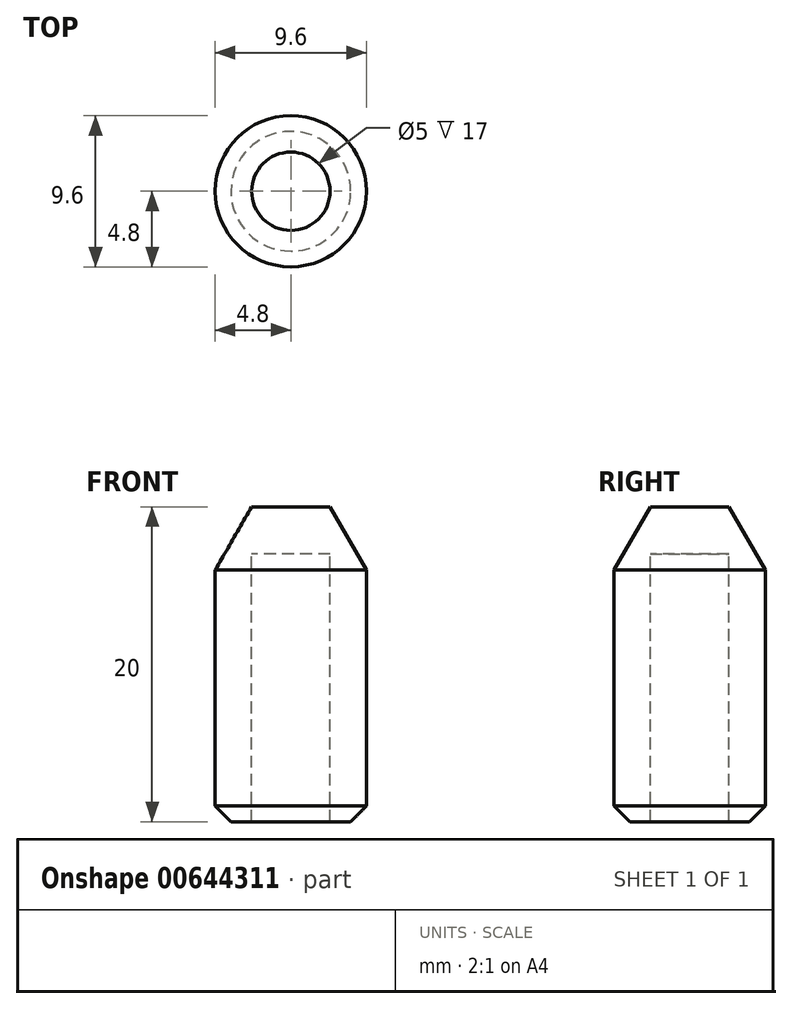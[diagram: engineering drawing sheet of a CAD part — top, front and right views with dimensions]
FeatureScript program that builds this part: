
annotation { "Feature Type Name" : "Feature", "Feature Type Description" : "" }
export const myFeature = defineFeature(function(context is Context, id is Id, definition is map)
    precondition{}
    {
        {
            var Q0;
            Q0=qCreatedBy(makeId("Right.planeOp"),FACE);
            var sketch = newSketch(context, id + "F0", { "sketchPlane" : qUnion([Q0])});
            skLineSegment(sketch, "E0", {"start": v(2.5, 0) * mm, "end": v(4.8, 0) * mm});
            skLineSegment(sketch, "E1", {"start": v(4.8, 0) * mm, "end": v(4.8, 20) * mm});
            skLineSegment(sketch, "E2", {"start": v(4.8, 20) * mm, "end": v(0, 20) * mm});
            skLineSegment(sketch, "E3", {"start": v(0, 42.87) * mm, "end": v(0, -12.23) * mm, "construction": true});
            skLineSegment(sketch, "E4", {"start": v(2.5, 0) * mm, "end": v(2.5, 17) * mm});
            skLineSegment(sketch, "E5", {"start": v(2.5, 17) * mm, "end": v(0, 17) * mm});
            skLineSegment(sketch, "E6", {"start": v(0, 20) * mm, "end": v(0, 17) * mm});
            skSolve(sketch);
        }
        {
            var Q0;
            Q0=qSketchRegion(id+"F0",true);
            var Q1;
            Q1=sQuery(id+"F0.wireOp",EDGE,"E3");
            revolve(context, id + "F1", {"entities" : qUnion([Q0]), "axis" : qUnion([Q1]), "revolveType" : RevolveType.FULL});
        }
        {
            var Q0;
            Q0=makeQuery(id+"F1.opRevolve","SWEPT_EDGE",EDGE,{"disambiguationData":[OSD([sQuery(id+"F0.wireOp",EDGE,"E0"),sQuery(id+"F0.wireOp",EDGE,"E1")])]});
            chamfer(context, id + "F2", {"entities" : qUnion([Q0]), "width" : 1 * mm, "tangentPropagation" : true});
        }
        {
            var Q0;
            Q0=makeQuery(id+"F1.opRevolve","SWEPT_EDGE",EDGE,{"disambiguationData":[OSD([sQuery(id+"F0.wireOp",EDGE,"E1"),sQuery(id+"F0.wireOp",EDGE,"E2")])]});
            chamfer(context, id + "F3", {"entities" : qUnion([Q0]), "chamferType" : ChamferType.OFFSET_ANGLE, "width" : 4 * mm, "oppositeDirection" : true, "angle" : 30 * degree, "tangentPropagation" : true});
        }
    });
